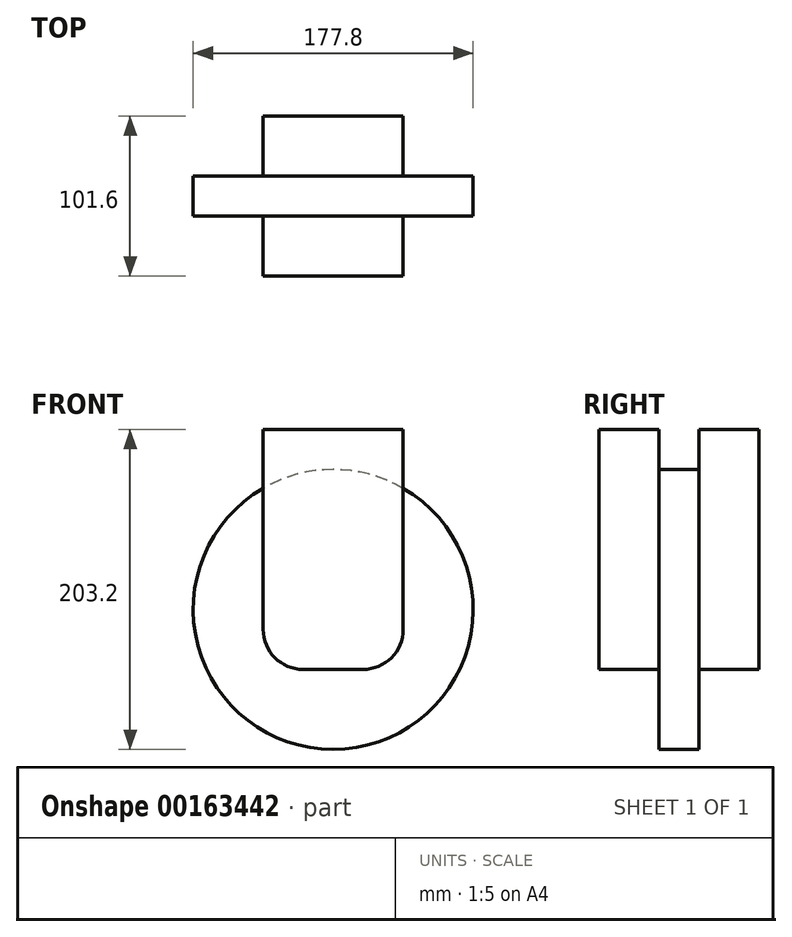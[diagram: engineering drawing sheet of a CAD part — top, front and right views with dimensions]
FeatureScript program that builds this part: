
annotation { "Feature Type Name" : "Feature", "Feature Type Description" : "" }
export const myFeature = defineFeature(function(context is Context, id is Id, definition is map)
    precondition{}
    {
        {
            var Q0;
            Q0=qCreatedBy(makeId("Front.planeOp"),FACE);
            var sketch = newSketch(context, id + "F0", { "sketchPlane" : qUnion([Q0])});
            skLineSegment(sketch, "E0", {"start": v(0, 0) * mm, "end": v(88.9, 0) * mm});
            skLineSegment(sketch, "E1", {"start": v(88.9, 0) * mm, "end": v(88.9, -127) * mm});
            skLineSegment(sketch, "E2", {"start": v(63.5, -152.4) * mm, "end": v(25.4, -152.4) * mm});
            skLineSegment(sketch, "E3", {"start": v(0, -127) * mm, "end": v(0, 0) * mm});
            skPoint(sketch, "E4.visualSharp", {"position": v(0, -152.4) * mm});
            skArc(sketch, "E4.filletArc", {"start": v(0, -127) * mm, "mid": v(7.44, -144.96) * mm, "end": v(25.4, -152.4) * mm});
            skPoint(sketch, "E5.visualSharp", {"position": v(88.9, -152.4) * mm});
            skArc(sketch, "E5.filletArc", {"start": v(63.5, -152.4) * mm, "mid": v(81.46, -144.96) * mm, "end": v(88.9, -127) * mm});
            skLineSegment(sketch, "E6", {"start": v(44.45, -152.4) * mm, "end": v(44.45, -114.3) * mm, "construction": true});
            skLineSegment(sketch, "E7", {"start": v(44.45, -114.3) * mm, "end": v(88.9, -114.3) * mm, "construction": true});
            skSolve(sketch);
        }
        {
            var Q0;
            Q0 = qSketchRegion(id + "F0", true);
            extrude(context, id + "F1", {"entities" : qUnion([Q0]), "depth" : 38.1 * mm});
        }
        {
            var Q0;
            Q0=makeQuery(id+"F1.opExtrude","CAP_FACE",FACE,{"disambiguationData":[OSD([sQuery(id+"F0.wireOp",EDGE,"E0"),sQuery(id+"F0.wireOp",EDGE,"E1"),sQuery(id+"F0.wireOp",EDGE,"E2"),sQuery(id+"F0.wireOp",EDGE,"E3"),sQuery(id+"F0.wireOp",EDGE,"E4.filletArc"),sQuery(id+"F0.wireOp",EDGE,"E5.filletArc")])],"isStart":false});
            var sketch = newSketch(context, id + "F2", { "sketchPlane" : qUnion([Q0])});
            skCircle(sketch, "E8", {"center": v(44.45, -114.3) * mm, "radius": 88.9 * mm});
            skSolve(sketch);
        }
        {
            var Q0;
            Q0 = qSketchRegion(id + "F2", true);
            extrude(context, id + "F3", {"entities" : qUnion([Q0]), "operationType" : NewBodyOperationType.ADD, "depth" : 25.4 * mm});
        }
        {
            var Q0;
            Q0=makeQuery(id+"F3.opExtrude","CAP_FACE",FACE,{"disambiguationData":[OSD([sQuery(id+"F2.wireOp",EDGE,"E8")])],"isStart":false});
            var sketch = newSketch(context, id + "F4", { "sketchPlane" : qUnion([Q0])});
            skLineSegment(sketch, "E9", {"start": v(0, 0) * mm, "end": v(88.9, 0) * mm});
            skLineSegment(sketch, "E10", {"start": v(88.9, 0) * mm, "end": v(88.9, -127) * mm});
            skLineSegment(sketch, "E11", {"start": v(63.5, -152.4) * mm, "end": v(25.4, -152.4) * mm});
            skLineSegment(sketch, "E12", {"start": v(0, -127) * mm, "end": v(0, 0) * mm});
            skPoint(sketch, "E13.visualSharp", {"position": v(0, -152.4) * mm});
            skArc(sketch, "E13.filletArc", {"start": v(0, -127) * mm, "mid": v(7.44, -144.96) * mm, "end": v(25.4, -152.4) * mm});
            skPoint(sketch, "E14.visualSharp", {"position": v(88.9, -152.4) * mm});
            skArc(sketch, "E14.filletArc", {"start": v(63.5, -152.4) * mm, "mid": v(81.46, -144.96) * mm, "end": v(88.9, -127) * mm});
            skLineSegment(sketch, "E15", {"start": v(44.45, -152.4) * mm, "end": v(44.45, -114.3) * mm, "construction": true});
            skLineSegment(sketch, "E16", {"start": v(44.45, -114.3) * mm, "end": v(88.9, -114.3) * mm, "construction": true});
            skSolve(sketch);
        }
        {
            var Q0;
            Q0 = qSketchRegion(id + "F4", true);
            extrude(context, id + "F5", {"entities" : qUnion([Q0]), "operationType" : NewBodyOperationType.ADD, "depth" : 38.1 * mm});
        }
    });
